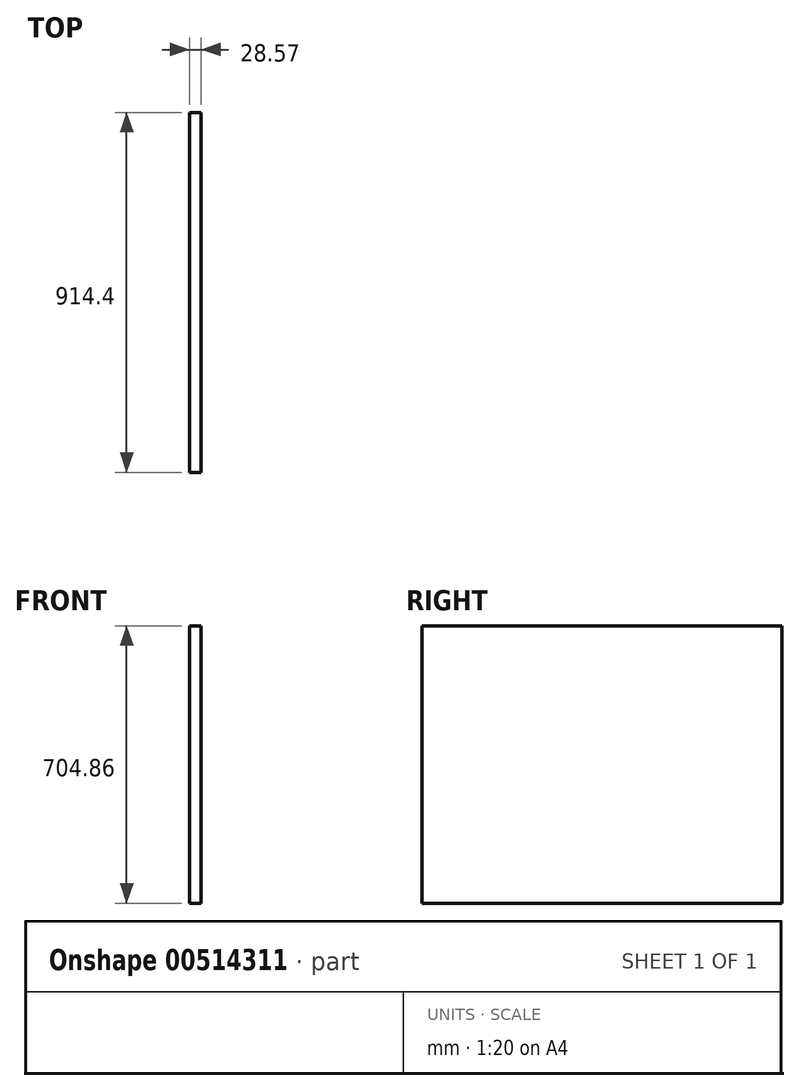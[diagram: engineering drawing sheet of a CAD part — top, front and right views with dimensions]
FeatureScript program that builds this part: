
annotation { "Feature Type Name" : "Feature", "Feature Type Description" : "" }
export const myFeature = defineFeature(function(context is Context, id is Id, definition is map)
    precondition{}
    {
        {
            var Q0;
            Q0=qCreatedBy(makeId("Right.planeOp"),FACE);
            var sketch = newSketch(context, id + "F0", { "sketchPlane" : qUnion([Q0])});
            skLineSegment(sketch, "E0.bottom", {"start": v(457.2, 352.43) * mm, "end": v(-457.2, 352.43) * mm});
            skLineSegment(sketch, "E0.top", {"start": v(457.2, -352.43) * mm, "end": v(-457.2, -352.43) * mm});
            skLineSegment(sketch, "E0.left", {"start": v(457.2, 352.43) * mm, "end": v(457.2, -352.42) * mm});
            skLineSegment(sketch, "E0.right", {"start": v(-457.2, 352.43) * mm, "end": v(-457.2, -352.43) * mm});
            skPoint(sketch, "E0.middle", {"position": v(0, 0) * mm});
            skSolve(sketch);
        }
        {
            var Q0;
            Q0=makeQuery(id+"F0.imprint","IMPRINT",FACE,{"disambiguationData":[TD([[makeQuery(id+"F0.imprint","IMPRINT",EDGE,{"derivedFrom":sQuery(id+"F0.wireOp",EDGE,"E0.bottom")}),1.0]])]});
            extrude(context, id + "F1", {"entities" : qUnion([Q0]), "depth" : 28.57 * mm});
        }
    });
